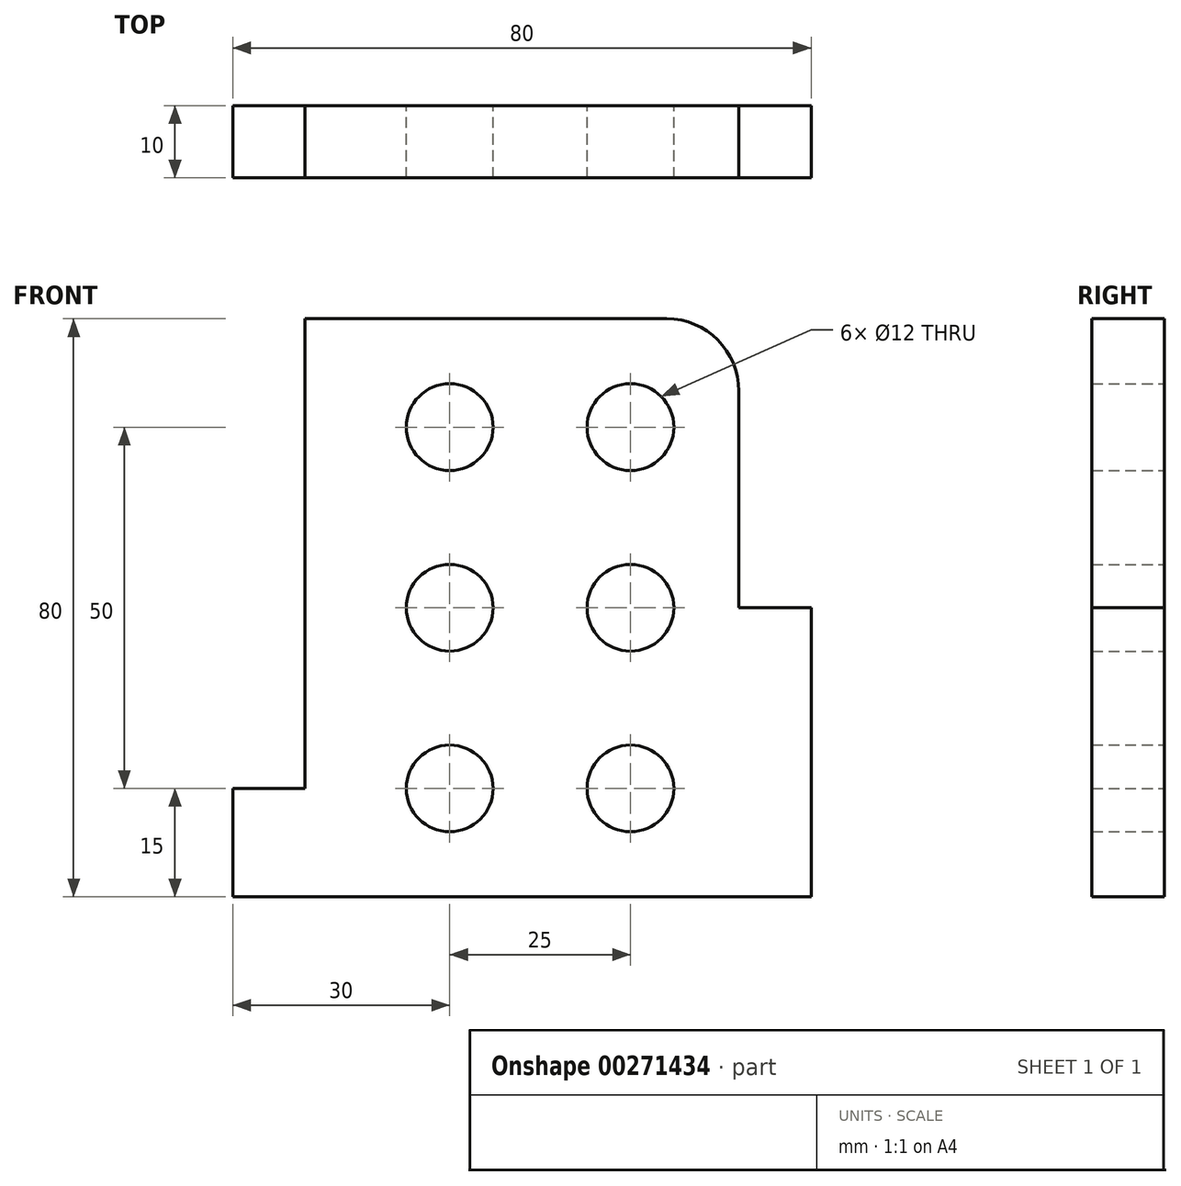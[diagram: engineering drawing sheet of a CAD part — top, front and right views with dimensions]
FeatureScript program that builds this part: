
annotation { "Feature Type Name" : "Feature", "Feature Type Description" : "" }
export const myFeature = defineFeature(function(context is Context, id is Id, definition is map)
    precondition{}
    {
        {
            var Q0;
            Q0=qCreatedBy(makeId("Front.planeOp"),FACE);
            var sketch = newSketch(context, id + "F0", { "sketchPlane" : qUnion([Q0])});
            skLineSegment(sketch, "E0", {"start": v(0, 0) * mm, "end": v(0, 15) * mm});
            skLineSegment(sketch, "E1", {"start": v(0, 15) * mm, "end": v(10, 15) * mm});
            skLineSegment(sketch, "E2", {"start": v(10, 15) * mm, "end": v(10, 80) * mm});
            skLineSegment(sketch, "E3", {"start": v(10, 80) * mm, "end": v(60, 80) * mm});
            skLineSegment(sketch, "E4", {"start": v(70, 70) * mm, "end": v(70, 40) * mm});
            skLineSegment(sketch, "E5", {"start": v(70, 40) * mm, "end": v(80, 40) * mm});
            skLineSegment(sketch, "E6", {"start": v(80, 40) * mm, "end": v(80, 0) * mm});
            skLineSegment(sketch, "E7", {"start": v(80, 0) * mm, "end": v(0, 0) * mm});
            skArc(sketch, "E8", {"start": v(70, 70) * mm, "mid": v(67.07, 77.07) * mm, "end": v(60, 80) * mm});
            skCircle(sketch, "E9", {"center": v(30, 15) * mm, "radius": 6 * mm});
            skCircle(sketch, "E10", {"center": v(55, 15) * mm, "radius": 6 * mm});
            skCircle(sketch, "E11", {"center": v(30, 40) * mm, "radius": 6 * mm});
            skCircle(sketch, "E12", {"center": v(55, 40) * mm, "radius": 6 * mm});
            skCircle(sketch, "E13", {"center": v(30, 65) * mm, "radius": 6 * mm});
            skLineSegment(sketch, "E14", {"start": v(10, 15) * mm, "end": v(10, 65) * mm});
            skCircle(sketch, "E15", {"center": v(55, 65) * mm, "radius": 6 * mm});
            skSolve(sketch);
        }
        {
            var Q0;
            Q0 = qSketchRegion(id + "F0", true);
            extrude(context, id + "F1", {"entities" : qUnion([Q0]), "depth" : 10 * mm});
        }
    });
